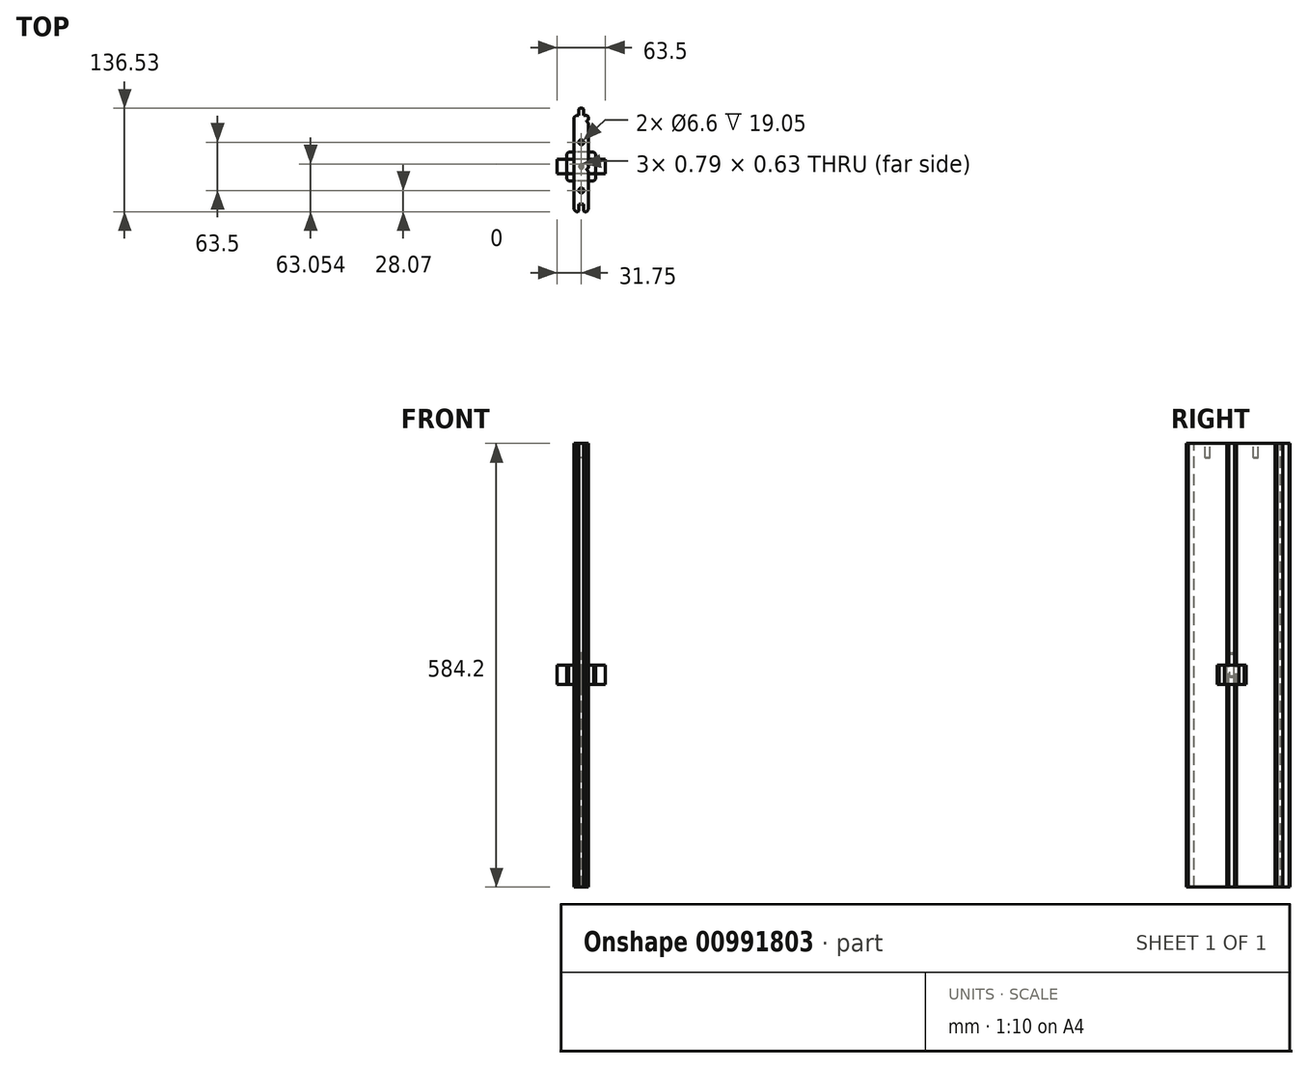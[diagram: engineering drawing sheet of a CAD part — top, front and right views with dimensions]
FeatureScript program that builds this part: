
annotation { "Feature Type Name" : "Feature", "Feature Type Description" : "" }
export const myFeature = defineFeature(function(context is Context, id is Id, definition is map)
    precondition{}
    {
        {
            var Q0;
            Q0=qCreatedBy(makeId("Top.planeOp"),FACE);
            var sketch = newSketch(context, id + "F0", { "sketchPlane" : qUnion([Q0])});
            skLineSegment(sketch, "E0", {"start": v(-3.18, -49.66) * mm, "end": v(3.17, -49.66) * mm});
            skLineSegment(sketch, "E1", {"start": v(3.17, -49.66) * mm, "end": v(3.17, -59.82) * mm});
            skLineSegment(sketch, "E2", {"start": v(3.17, -59.82) * mm, "end": v(6.7, -59.82) * mm});
            skLineSegment(sketch, "E3", {"start": v(9.52, -57) * mm, "end": v(9.52, -6.5) * mm});
            skLineSegment(sketch, "E4", {"start": v(9.52, -6.5) * mm, "end": v(6.7, -3.68) * mm});
            skLineSegment(sketch, "E5", {"start": v(6.7, 3.68) * mm, "end": v(9.52, 6.5) * mm});
            skLineSegment(sketch, "E6", {"start": v(9.52, 6.5) * mm, "end": v(9.52, 57) * mm});
            skLineSegment(sketch, "E7", {"start": v(6.7, 59.82) * mm, "end": v(9.52, 57) * mm});
            skLineSegment(sketch, "E8", {"start": v(6.7, 67.18) * mm, "end": v(3.17, 67.18) * mm});
            skLineSegment(sketch, "E9", {"start": v(3.17, 67.18) * mm, "end": v(3.17, 76.7) * mm});
            skLineSegment(sketch, "E10", {"start": v(3.17, 76.7) * mm, "end": v(-3.18, 76.7) * mm});
            skLineSegment(sketch, "E11", {"start": v(-3.18, 76.7) * mm, "end": v(-3.18, 67.18) * mm});
            skLineSegment(sketch, "E12", {"start": v(-3.18, 67.18) * mm, "end": v(-6.7, 67.18) * mm});
            skLineSegment(sketch, "E13", {"start": v(-9.53, 64.36) * mm, "end": v(-9.52, -57) * mm});
            skLineSegment(sketch, "E14", {"start": v(-6.7, -59.82) * mm, "end": v(-3.18, -59.82) * mm});
            skLineSegment(sketch, "E15", {"start": v(-3.18, -59.82) * mm, "end": v(-3.18, -49.66) * mm});
            skLineSegment(sketch, "E16", {"start": v(6.7, -59.82) * mm, "end": v(9.52, -57) * mm});
            skArc(sketch, "E17", {"start": v(6.7, -3.68) * mm, "mid": v(9.53, 0) * mm, "end": v(6.7, 3.68) * mm});
            skArc(sketch, "E18", {"start": v(6.7, 59.82) * mm, "mid": v(9.52, 63.5) * mm, "end": v(6.7, 67.18) * mm});
            skLineSegment(sketch, "E19", {"start": v(-9.53, 64.36) * mm, "end": v(-6.7, 67.18) * mm});
            skLineSegment(sketch, "E20", {"start": v(-9.53, -57) * mm, "end": v(-6.7, -59.82) * mm});
            skLineSegment(sketch, "E21", {"start": v(5.72, 0) * mm, "end": v(6.7, 3.68) * mm, "construction": true});
            skSolve(sketch);
        }
        {
            var Q0;
            Q0=qSketchRegion(id+"F0",true);
            extrude(context, id + "F1", {"entities" : qUnion([Q0]), "endBound" : BoundingType.SYMMETRIC, "oppositeDirection" : true, "depth" : 584.2 * mm, "offsetDistance" : 25.4 * mm});
        }
        {
            var Q0;
            Q0=makeQuery(id+"F1.opExtrude","SWEPT_EDGE",EDGE,{"disambiguationData":[OSD([sQuery(id+"F0.wireOp",EDGE,"E10"),sQuery(id+"F0.wireOp",EDGE,"E11")])]});
            var Q1;
            Q1=makeQuery(id+"F1.opExtrude","SWEPT_EDGE",EDGE,{"disambiguationData":[OSD([sQuery(id+"F0.wireOp",EDGE,"E9"),sQuery(id+"F0.wireOp",EDGE,"E10")])]});
            var Q2;
            Q2=makeQuery(id+"F1.opExtrude","SWEPT_EDGE",EDGE,{"disambiguationData":[OSD([sQuery(id+"F0.wireOp",EDGE,"E14"),sQuery(id+"F0.wireOp",EDGE,"E15")])]});
            var Q3;
            Q3=makeQuery(id+"F1.opExtrude","SWEPT_EDGE",EDGE,{"disambiguationData":[OSD([sQuery(id+"F0.wireOp",EDGE,"E1"),sQuery(id+"F0.wireOp",EDGE,"E2")])]});
            chamfer(context, id + "F2", {"entities" : qUnion([Q0, Q1, Q2, Q3]), "width" : 1.27 * mm, "tangentPropagation" : true});
        }
        {
            var Q0;
            Q0=makeQuery(id+"F1.opExtrude","CAP_FACE",FACE,{"disambiguationData":[OSD([sQuery(id+"F0.wireOp",EDGE,"E0"),sQuery(id+"F0.wireOp",EDGE,"E1"),sQuery(id+"F0.wireOp",EDGE,"E2"),sQuery(id+"F0.wireOp",EDGE,"E3"),sQuery(id+"F0.wireOp",EDGE,"E4"),sQuery(id+"F0.wireOp",EDGE,"E5"),sQuery(id+"F0.wireOp",EDGE,"E6"),sQuery(id+"F0.wireOp",EDGE,"E7"),sQuery(id+"F0.wireOp",EDGE,"E8"),sQuery(id+"F0.wireOp",EDGE,"E9"),sQuery(id+"F0.wireOp",EDGE,"E10"),sQuery(id+"F0.wireOp",EDGE,"E11"),sQuery(id+"F0.wireOp",EDGE,"E12"),sQuery(id+"F0.wireOp",EDGE,"E13"),sQuery(id+"F0.wireOp",EDGE,"E14"),sQuery(id+"F0.wireOp",EDGE,"E15"),sQuery(id+"F0.wireOp",EDGE,"E16"),sQuery(id+"F0.wireOp",EDGE,"E17"),sQuery(id+"F0.wireOp",EDGE,"E18"),sQuery(id+"F0.wireOp",EDGE,"E19"),sQuery(id+"F0.wireOp",EDGE,"E20")])],"isStart":true});
            var sketch = newSketch(context, id + "F3", { "sketchPlane" : qUnion([Q0])});
            skCircle(sketch, "E22", {"center": v(0, 31.75) * mm, "radius": 3.3 * mm});
            skPoint(sketch, "E22.centerSnap0", {"position": v(9.52, 31.75) * mm});
            skCircle(sketch, "E23", {"center": v(0, -31.75) * mm, "radius": 3.3 * mm});
            skPoint(sketch, "E23.centerSnap0", {"position": v(9.52, -31.75) * mm});
            skSolve(sketch);
        }
        {
            var Q0;
            Q0 = qSketchRegion(id + "F3", true);
            extrude(context, id + "F4", {"entities" : qUnion([Q0]), "operationType" : NewBodyOperationType.REMOVE, "oppositeDirection" : true, "depth" : 19.05 * mm, "offsetDistance" : 25.4 * mm});
        }
        {
            var Q0;
            Q0=qCreatedBy(makeId("Top.planeOp"),FACE);
            var sketch = newSketch(context, id + "F5", { "sketchPlane" : qUnion([Q0])});
            skLineSegment(sketch, "E24.bottom", {"start": v(19.05, 9.53) * mm, "end": v(-19.05, 9.53) * mm});
            skLineSegment(sketch, "E24.top", {"start": v(19.05, -9.53) * mm, "end": v(-19.05, -9.53) * mm});
            skLineSegment(sketch, "E24.left", {"start": v(19.05, 9.53) * mm, "end": v(19.05, -9.53) * mm});
            skLineSegment(sketch, "E24.right", {"start": v(-19.05, 9.53) * mm, "end": v(-19.05, -9.53) * mm});
            skPoint(sketch, "E24.middle", {"position": v(0, 0) * mm});
            skSolve(sketch);
        }
        {
            var Q0;
            Q0=makeQuery(id+"F5.imprint","IMPRINT",FACE,{"disambiguationData":[TD([[makeQuery(id+"F5.imprint","IMPRINT",EDGE,{"derivedFrom":sQuery(id+"F5.wireOp",EDGE,"E24.bottom")}),1.0]])]});
            extrude(context, id + "F6", {"entities" : qUnion([Q0]), "oppositeDirection" : true, "depth" : 25.4 * mm, "offsetDistance" : 25.4 * mm});
        }
        {
            var Q0;
            Q0=makeQuery(id+"F6.opExtrude","SWEPT_EDGE",EDGE,{"disambiguationData":[OSD([sQuery(id+"F5.wireOp",EDGE,"E24.top"),sQuery(id+"F5.wireOp",EDGE,"E24.left")])]});
            var Q1;
            Q1=makeQuery(id+"F6.opExtrude","SWEPT_EDGE",EDGE,{"disambiguationData":[OSD([sQuery(id+"F5.wireOp",EDGE,"E24.top"),sQuery(id+"F5.wireOp",EDGE,"E24.right")])]});
            chamfer(context, id + "F7", {"entities" : qUnion([Q0, Q1]), "width" : 2.54 * mm, "tangentPropagation" : true});
        }
        {
            var Q0;
            Q0=qCreatedBy(makeId("Top.planeOp"),FACE);
            var sketch = newSketch(context, id + "F8", { "sketchPlane" : qUnion([Q0])});
            skLineSegment(sketch, "E25.bottom", {"start": v(19.05, -19.05) * mm, "end": v(-19.05, -19.05) * mm});
            skLineSegment(sketch, "E25.top", {"start": v(19.05, 19.05) * mm, "end": v(-19.05, 19.05) * mm});
            skLineSegment(sketch, "E25.left", {"start": v(19.05, -19.05) * mm, "end": v(19.05, 19.05) * mm});
            skLineSegment(sketch, "E25.right", {"start": v(-19.05, -19.05) * mm, "end": v(-19.05, 19.05) * mm});
            skPoint(sketch, "E25.middle", {"position": v(0, 0) * mm});
            skSolve(sketch);
        }
        {
            var Q0;
            Q0=makeQuery(id+"F8.imprint","IMPRINT",FACE,{"disambiguationData":[TD([[makeQuery(id+"F8.imprint","IMPRINT",EDGE,{"derivedFrom":sQuery(id+"F8.wireOp",EDGE,"E25.bottom")}),-1.0]])]});
            extrude(context, id + "F9", {"entities" : qUnion([Q0]), "oppositeDirection" : true, "depth" : 25.4 * mm, "offsetDistance" : 25.4 * mm});
        }
        {
            var Q0;
            Q0=makeQuery(id+"F9.opExtrude","SWEPT_EDGE",EDGE,{"disambiguationData":[OSD([sQuery(id+"F8.wireOp",EDGE,"E25.top"),sQuery(id+"F8.wireOp",EDGE,"E25.left")])]});
            var Q1;
            Q1=makeQuery(id+"F9.opExtrude","SWEPT_EDGE",EDGE,{"disambiguationData":[OSD([sQuery(id+"F8.wireOp",EDGE,"E25.bottom"),sQuery(id+"F8.wireOp",EDGE,"E25.left")])]});
            var Q2;
            Q2=makeQuery(id+"F9.opExtrude","SWEPT_EDGE",EDGE,{"disambiguationData":[OSD([sQuery(id+"F8.wireOp",EDGE,"E25.bottom"),sQuery(id+"F8.wireOp",EDGE,"E25.right")])]});
            var Q3;
            Q3=makeQuery(id+"F9.opExtrude","SWEPT_EDGE",EDGE,{"disambiguationData":[OSD([sQuery(id+"F8.wireOp",EDGE,"E25.top"),sQuery(id+"F8.wireOp",EDGE,"E25.right")])]});
            chamfer(context, id + "F10", {"entities" : qUnion([Q0, Q1, Q2, Q3]), "width" : 2.54 * mm});
        }
        {
            var Q0;
            Q0=qCreatedBy(makeId("Top.planeOp"),FACE);
            var sketch = newSketch(context, id + "F11", { "sketchPlane" : qUnion([Q0])});
            skLineSegment(sketch, "E26.bottom", {"start": v(31.75, -9.52) * mm, "end": v(-31.75, -9.53) * mm});
            skLineSegment(sketch, "E26.top", {"start": v(31.75, 9.53) * mm, "end": v(-31.75, 9.53) * mm});
            skLineSegment(sketch, "E26.left", {"start": v(31.75, -9.52) * mm, "end": v(31.75, 9.53) * mm});
            skLineSegment(sketch, "E26.right", {"start": v(-31.75, -9.53) * mm, "end": v(-31.75, 9.53) * mm});
            skPoint(sketch, "E26.middle", {"position": v(0, 0) * mm});
            skSolve(sketch);
        }
        {
            var Q0;
            Q0=makeQuery(id+"F11.imprint","IMPRINT",FACE,{"disambiguationData":[TD([[makeQuery(id+"F11.imprint","IMPRINT",EDGE,{"derivedFrom":sQuery(id+"F11.wireOp",EDGE,"E26.bottom")}),-1.0]])]});
            extrude(context, id + "F12", {"entities" : qUnion([Q0]), "oppositeDirection" : true, "depth" : 25.4 * mm, "offsetDistance" : 25.4 * mm});
        }
        {
            var Q0;
            Q0=qCreatedBy(makeId("Top.planeOp"),FACE);
            var sketch = newSketch(context, id + "F13", { "sketchPlane" : qUnion([Q0])});
            skCircle(sketch, "E27", {"center": v(0, 0) * mm, "radius": 3.18 * mm});
            skSolve(sketch);
        }
        {
            var Q0;
            Q0 = qSketchRegion(id + "F13", true);
            extrude(context, id + "F14", {"entities" : qUnion([Q0]), "endBound" : BoundingType.SYMMETRIC, "depth" : 31.75 * mm, "offsetDistance" : 25.4 * mm});
        }
        {
            var Q0;
            Q0=makeQuery(id+"F14.opExtrude","CAP_FACE",FACE,{"disambiguationData":[OSD([sQuery(id+"F13.wireOp",EDGE,"E27")])],"isStart":false});
            var sketch = newSketch(context, id + "F15", { "sketchPlane" : qUnion([Q0])});
            skLineSegment(sketch, "E28", {"start": v(0, 2.92) * mm, "end": v(0, 0) * mm, "construction": true});
            skLineSegment(sketch, "E29", {"start": v(-0.4, 3.15) * mm, "end": v(0, 3.55) * mm});
            skLineSegment(sketch, "E30", {"start": v(0, 3.55) * mm, "end": v(0.4, 3.15) * mm});
            skLineSegment(sketch, "E31", {"start": v(-0.4, 3.15) * mm, "end": v(0, 2.92) * mm});
            skLineSegment(sketch, "E32", {"start": v(0.4, 3.15) * mm, "end": v(0, 2.92) * mm});
            skSolve(sketch);
        }
        {
            var Q0;
            Q0=makeQuery(id+"F14.opExtrude","CAP_EDGE",EDGE,{"disambiguationData":[OSD([sQuery(id+"F13.wireOp",EDGE,"E27")])],"isStart":false});
            var Q1;
            Q1=makeQuery(id+"F14.opExtrude","CAP_EDGE",EDGE,{"disambiguationData":[OSD([sQuery(id+"F13.wireOp",EDGE,"E27")])],"isStart":true});
            chamfer(context, id + "F16", {"entities" : qUnion([Q0, Q1]), "width" : 1.52 * mm, "tangentPropagation" : true});
        }
        {
            var Q0;
            Q0 = qSketchRegion(id + "F15", true);
            extrude(context, id + "F17", {"entities" : qUnion([Q0]), "operationType" : NewBodyOperationType.REMOVE, "endBound" : BoundingType.THROUGH_ALL, "oppositeDirection" : true, "depth" : 25.4 * mm, "offsetDistance" : 25.4 * mm});
        }
    });
